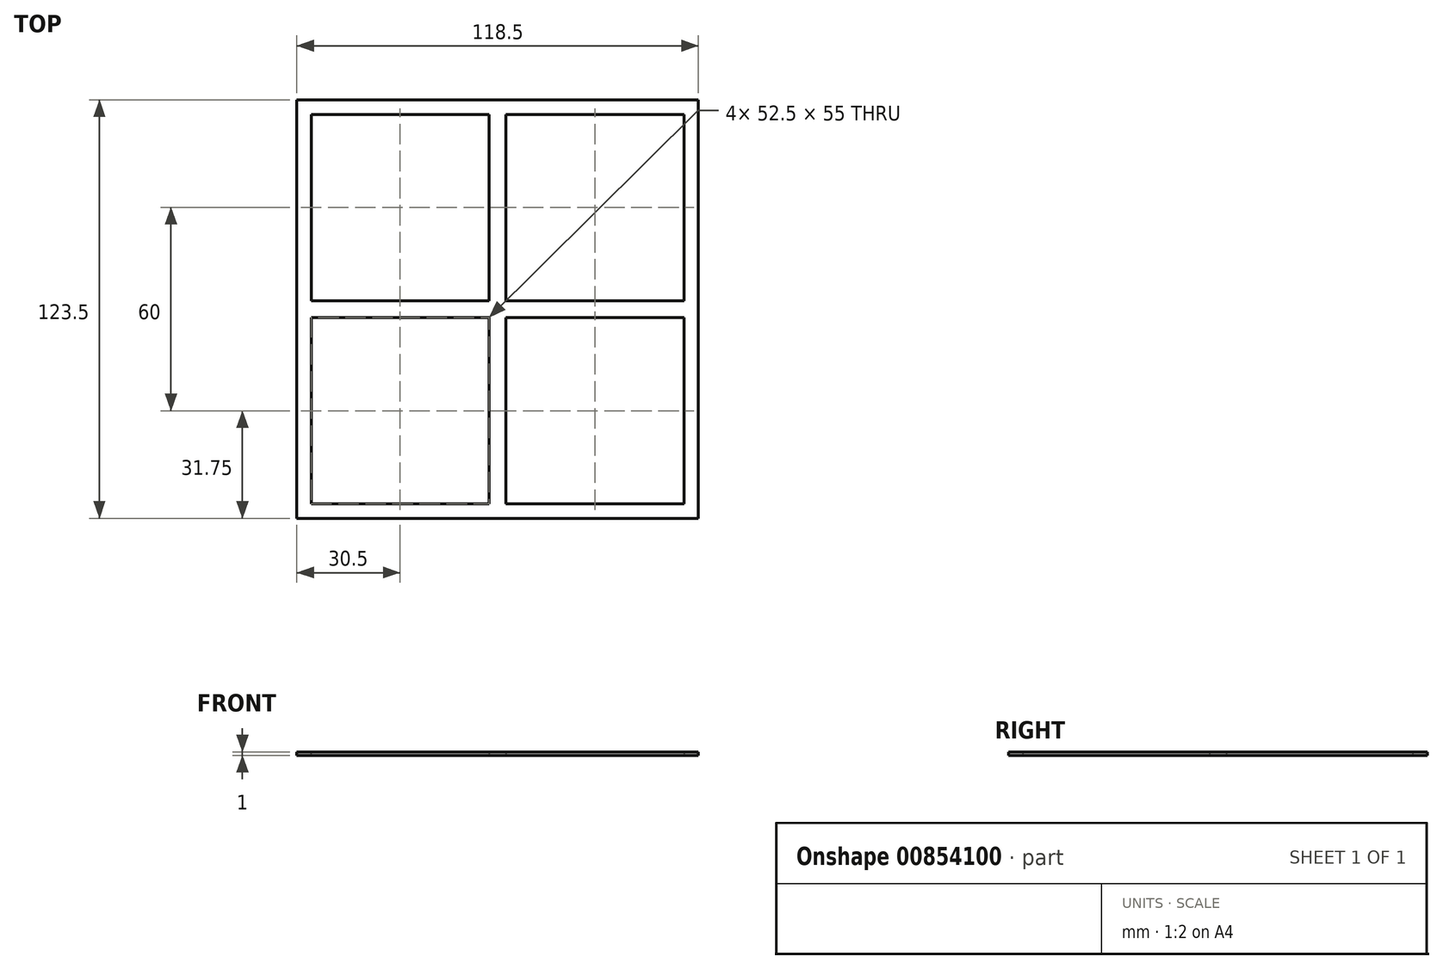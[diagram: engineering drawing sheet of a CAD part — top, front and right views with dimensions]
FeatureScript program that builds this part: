
annotation { "Feature Type Name" : "Feature", "Feature Type Description" : "" }
export const myFeature = defineFeature(function(context is Context, id is Id, definition is map)
    precondition{}
    {
        {
            var Q0;
            Q0=qCreatedBy(makeId("Top.planeOp"),FACE);
            var sketch = newSketch(context, id + "F0", { "sketchPlane" : qUnion([Q0])});
            skLineSegment(sketch, "E0.bottom", {"start": v(-59.25, 61.75) * mm, "end": v(59.25, 61.75) * mm});
            skLineSegment(sketch, "E0.top", {"start": v(-59.25, -61.75) * mm, "end": v(59.25, -61.75) * mm});
            skLineSegment(sketch, "E0.left", {"start": v(-59.25, 61.75) * mm, "end": v(-59.25, -61.75) * mm});
            skLineSegment(sketch, "E0.right", {"start": v(59.25, 61.75) * mm, "end": v(59.25, -61.75) * mm});
            skPoint(sketch, "E0.middle", {"position": v(0, 0) * mm});
            skSolve(sketch);
        }
        {
            var Q0;
            Q0=makeQuery(id+"F0.imprint","IMPRINT",FACE,{"disambiguationData":[TD([[makeQuery(id+"F0.imprint","IMPRINT",EDGE,{"derivedFrom":sQuery(id+"F0.wireOp",EDGE,"E0.bottom")}),-1.0]])]});
            extrude(context, id + "F1", {"entities" : qUnion([Q0]), "depth" : 1 * mm, "offsetDistance" : 25 * mm});
        }
        {
            var Q0;
            Q0=makeQuery(id+"F1.opExtrude","CAP_FACE",FACE,{"disambiguationData":[OSD([sQuery(id+"F0.wireOp",EDGE,"E0.bottom"),sQuery(id+"F0.wireOp",EDGE,"E0.top"),sQuery(id+"F0.wireOp",EDGE,"E0.left"),sQuery(id+"F0.wireOp",EDGE,"E0.right")])],"isStart":false});
            var sketch = newSketch(context, id + "F2", { "sketchPlane" : qUnion([Q0])});
            skLineSegment(sketch, "E1.bottom", {"start": v(55, 57.5) * mm, "end": v(-55, 57.5) * mm});
            skLineSegment(sketch, "E1.top", {"start": v(55, -57.5) * mm, "end": v(-55, -57.5) * mm});
            skLineSegment(sketch, "E1.left", {"start": v(55, 57.5) * mm, "end": v(55, -57.5) * mm});
            skLineSegment(sketch, "E1.right", {"start": v(-55, 57.5) * mm, "end": v(-55, -57.5) * mm});
            skPoint(sketch, "E1.middle", {"position": v(0, 0) * mm});
            skSolve(sketch);
        }
        {
            var Q0;
            Q0=makeQuery(id+"F2.imprint","IMPRINT",FACE,{"disambiguationData":[TD([[makeQuery(id+"F2.imprint","IMPRINT",EDGE,{"derivedFrom":sQuery(id+"F2.wireOp",EDGE,"E1.bottom")}),1.0]])]});
            extrude(context, id + "F3", {"entities" : qUnion([Q0]), "operationType" : NewBodyOperationType.REMOVE, "oppositeDirection" : true, "depth" : 25 * mm, "offsetDistance" : 25 * mm});
        }
        {
            var Q0;
            Q0=qCreatedBy(makeId("Top.planeOp"),FACE);
            var sketch = newSketch(context, id + "F4", { "sketchPlane" : qUnion([Q0])});
            skLineSegment(sketch, "E2.bottom", {"start": v(2.5, 57.5) * mm, "end": v(-2.5, 57.5) * mm});
            skLineSegment(sketch, "E2.top", {"start": v(2.5, -57.5) * mm, "end": v(-2.5, -57.5) * mm});
            skLineSegment(sketch, "E2.left", {"start": v(2.5, 57.5) * mm, "end": v(2.5, 2.5) * mm});
            skLineSegment(sketch, "E2.right", {"start": v(-2.5, 57.5) * mm, "end": v(-2.5, 2.5) * mm});
            skPoint(sketch, "E2.middle", {"position": v(0, 0) * mm});
            skLineSegment(sketch, "E3.bottom", {"start": v(55, 2.5) * mm, "end": v(2.5, 2.5) * mm});
            skLineSegment(sketch, "E3.top", {"start": v(55, -2.5) * mm, "end": v(2.5, -2.5) * mm});
            skLineSegment(sketch, "E3.left", {"start": v(55, 2.5) * mm, "end": v(55, -2.5) * mm});
            skLineSegment(sketch, "E3.right", {"start": v(-55, 2.5) * mm, "end": v(-55, -2.5) * mm});
            skLineSegment(sketch, "E4.trimOffspring", {"start": v(-2.5, -2.5) * mm, "end": v(-2.5, -57.5) * mm});
            skLineSegment(sketch, "E5.trimOffspring", {"start": v(-2.5, 2.5) * mm, "end": v(-55, 2.5) * mm});
            skLineSegment(sketch, "E6.trimOffspring", {"start": v(2.5, -2.5) * mm, "end": v(2.5, -57.5) * mm});
            skLineSegment(sketch, "E7.trimOffspring", {"start": v(-2.5, -2.5) * mm, "end": v(-55, -2.5) * mm});
            skSolve(sketch);
        }
        {
            var Q0;
            Q0 = qSketchRegion(id + "F4", true);
            extrude(context, id + "F5", {"entities" : qUnion([Q0]), "operationType" : NewBodyOperationType.ADD, "depth" : 1 * mm, "offsetDistance" : 25 * mm});
        }
    });
